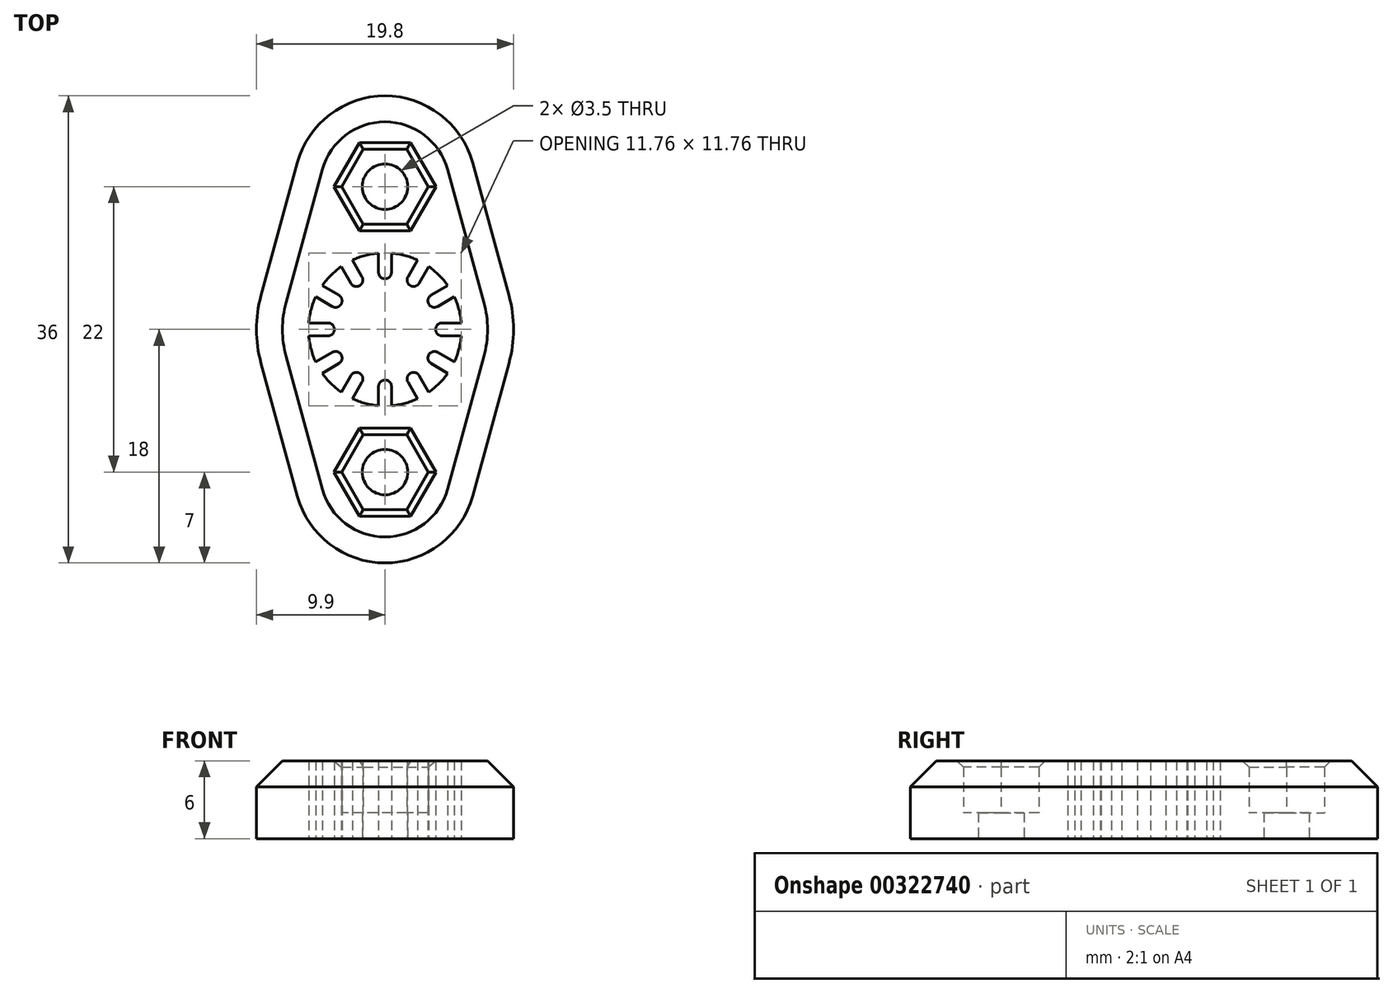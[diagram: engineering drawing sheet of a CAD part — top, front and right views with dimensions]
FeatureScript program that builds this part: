
annotation { "Feature Type Name" : "Feature", "Feature Type Description" : "" }
export const myFeature = defineFeature(function(context is Context, id is Id, definition is map)
    precondition{}
    {
        {
            assignVariable(context, id + "F0", {"name" : "teeth", "anyValue" : 12});
        }
        {
            assignVariable(context, id + "F1", {"name" : "height", "anyValue" : 6});
        }
        {
            var Q0;
            Q0=qCreatedBy(makeId("Top.planeOp"),FACE);
            var sketch = newSketch(context, id + "F2", { "sketchPlane" : qUnion([Q0])});
            skCircle(sketch, "E0", {"center": v(0, 0) * mm, "radius": 5.9 * mm});
            skArc(sketch, "E1", {"start": v(9.55, -2.61) * mm, "mid": v(9.9, 0) * mm, "end": v(9.55, 2.61) * mm});
            skArc(sketch, "E2", {"start": v(-6.75, 12.85) * mm, "mid": v(-4.25, 16.56) * mm, "end": v(0, 18) * mm});
            skLineSegment(sketch, "E3", {"start": v(-9.55, 2.6) * mm, "end": v(-6.75, 12.85) * mm});
            skArc(sketch, "E4.MirrorCS", {"start": v(6.75, 12.85) * mm, "mid": v(4.25, 16.56) * mm, "end": v(0, 18) * mm});
            skLineSegment(sketch, "E5.MirrorCS", {"start": v(9.55, 2.6) * mm, "end": v(6.75, 12.85) * mm});
            skLineSegment(sketch, "E6.MirrorCS", {"start": v(-9.55, -2.6) * mm, "end": v(-6.75, -12.85) * mm});
            skArc(sketch, "E7.MirrorCS", {"start": v(-6.75, -12.85) * mm, "mid": v(-4.25, -16.56) * mm, "end": v(0, -18) * mm});
            skArc(sketch, "E8.MirrorCS", {"start": v(6.75, -12.85) * mm, "mid": v(4.25, -16.56) * mm, "end": v(0, -18) * mm});
            skLineSegment(sketch, "E9.MirrorCS", {"start": v(9.55, -2.6) * mm, "end": v(6.75, -12.85) * mm});
            skArc(sketch, "E10.trimOffspring", {"start": v(-9.55, 2.61) * mm, "mid": v(-9.9, 0) * mm, "end": v(-9.55, -2.61) * mm});
            skCircle(sketch, "E11", {"center": v(0, 11) * mm, "radius": 1.75 * mm});
            skCircle(sketch, "E12.cCircle", {"center": v(0, 11) * mm, "radius": 2.9 * mm, "construction": true});
            skLineSegment(sketch, "E12.0", {"start": v(1.67, 8.1) * mm, "end": v(-1.67, 8.1) * mm});
            skLineSegment(sketch, "E12.1", {"start": v(-1.67, 8.1) * mm, "end": v(-3.35, 11) * mm});
            skLineSegment(sketch, "E12.2", {"start": v(-3.35, 11) * mm, "end": v(-1.67, 13.9) * mm});
            skLineSegment(sketch, "E12.3", {"start": v(-1.67, 13.9) * mm, "end": v(1.67, 13.9) * mm});
            skLineSegment(sketch, "E12.4", {"start": v(1.67, 13.9) * mm, "end": v(3.35, 11) * mm});
            skLineSegment(sketch, "E12.5", {"start": v(3.35, 11) * mm, "end": v(1.67, 8.1) * mm});
            skPoint(sketch, "E12.0.midPoint", {"position": v(0, 8.1) * mm});
            skLineSegment(sketch, "E13.MirrorCS", {"start": v(-1.67, -13.9) * mm, "end": v(1.67, -13.9) * mm});
            skLineSegment(sketch, "E14.MirrorCS", {"start": v(3.35, -11) * mm, "end": v(1.67, -8.1) * mm});
            skPoint(sketch, "E15.MirrorP", {"position": v(0, -8.1) * mm});
            skCircle(sketch, "E16.MirrorC", {"center": v(0, -11) * mm, "radius": 2.9 * mm, "construction": true});
            skCircle(sketch, "E17.MirrorC", {"center": v(0, -11) * mm, "radius": 1.75 * mm});
            skLineSegment(sketch, "E18.MirrorCS", {"start": v(1.67, -13.9) * mm, "end": v(3.35, -11) * mm});
            skLineSegment(sketch, "E19.MirrorCS", {"start": v(-1.67, -8.1) * mm, "end": v(-3.35, -11) * mm});
            skLineSegment(sketch, "E20.MirrorCS", {"start": v(-3.35, -11) * mm, "end": v(-1.67, -13.9) * mm});
            skLineSegment(sketch, "E21.MirrorCS", {"start": v(1.67, -8.1) * mm, "end": v(-1.67, -8.1) * mm});
            skSolve(sketch);
        }
        {
            var Q0;
            Q0=makeQuery(id+"F2.imprint","IMPRINT",FACE,{"disambiguationData":[TD([[makeQuery(id+"F2.imprint","IMPRINT",EDGE,{"derivedFrom":sQuery(id+"F2.wireOp",EDGE,"E0")}),-1.0]])]});
            extrude(context, id + "F3", {"entities" : qUnion([Q0]), "depth" : (getVariable(context, 'height')) * mm, "offsetDistance" : 25 * mm});
        }
        {
            var Q0;
            Q0=makeQuery(id+"F2.imprint","IMPRINT",FACE,{"disambiguationData":[TD([[makeQuery(id+"F2.imprint","IMPRINT",EDGE,{"derivedFrom":sQuery(id+"F2.wireOp",EDGE,"E11")}),-1.0]])]});
            var Q1;
            Q1=makeQuery(id+"F2.imprint","IMPRINT",FACE,{"disambiguationData":[TD([[makeQuery(id+"F2.imprint","IMPRINT",EDGE,{"derivedFrom":sQuery(id+"F2.wireOp",EDGE,"E13.MirrorCS")}),1.0]])]});
            extrude(context, id + "F4", {"entities" : qUnion([Q0, Q1]), "operationType" : NewBodyOperationType.ADD, "depth" : 2 * mm, "offsetDistance" : 25 * mm});
        }
        {
            var Q0;
            Q0=qCreatedBy(makeId("Top.planeOp"),FACE);
            var sketch = newSketch(context, id + "F5", { "sketchPlane" : qUnion([Q0])});
            skArc(sketch, "E22", {"start": v(0.5, -4.4) * mm, "mid": v(0, -3.9) * mm, "end": v(-0.5, -4.4) * mm});
            skLineSegment(sketch, "E23", {"start": v(0.5, -4.4) * mm, "end": v(0.5, -5.88) * mm});
            skLineSegment(sketch, "E24.MirrorCS", {"start": v(-0.5, -4.4) * mm, "end": v(-0.5, -5.88) * mm});
            skPoint(sketch, "E25", {"position": v(0, -5.9) * mm});
            skArc(sketch, "E26", {"start": v(-0.5, -5.88) * mm, "mid": v(0, -5.9) * mm, "end": v(0.5, -5.88) * mm});
            skPoint(sketch, "E27", {"position": v(0, -3.9) * mm});
            skSolve(sketch);
        }
        {
            var Q0;
            Q0=makeQuery(id+"F5.imprint","IMPRINT",FACE,{"disambiguationData":[TD([[makeQuery(id+"F5.imprint","IMPRINT",EDGE,{"derivedFrom":sQuery(id+"F5.wireOp",EDGE,"E22")}),1.0]])]});
            var Q1;
            Q1=makeQuery(id+"F3.opExtrude","CAP_FACE",FACE,{"disambiguationData":[OSD([sQuery(id+"F2.wireOp",EDGE,"E0"),sQuery(id+"F2.wireOp",EDGE,"E1"),sQuery(id+"F2.wireOp",EDGE,"E2"),sQuery(id+"F2.wireOp",EDGE,"E3"),sQuery(id+"F2.wireOp",EDGE,"E4.MirrorCS"),sQuery(id+"F2.wireOp",EDGE,"E5.MirrorCS"),sQuery(id+"F2.wireOp",EDGE,"E6.MirrorCS"),sQuery(id+"F2.wireOp",EDGE,"E7.MirrorCS"),sQuery(id+"F2.wireOp",EDGE,"E8.MirrorCS"),sQuery(id+"F2.wireOp",EDGE,"E9.MirrorCS"),sQuery(id+"F2.wireOp",EDGE,"E10.trimOffspring"),sQuery(id+"F2.wireOp",EDGE,"E12.0"),sQuery(id+"F2.wireOp",EDGE,"E12.1"),sQuery(id+"F2.wireOp",EDGE,"E12.2"),sQuery(id+"F2.wireOp",EDGE,"E12.3"),sQuery(id+"F2.wireOp",EDGE,"E12.4"),sQuery(id+"F2.wireOp",EDGE,"E12.5"),sQuery(id+"F2.wireOp",EDGE,"E13.MirrorCS"),sQuery(id+"F2.wireOp",EDGE,"E14.MirrorCS"),sQuery(id+"F2.wireOp",EDGE,"E18.MirrorCS"),sQuery(id+"F2.wireOp",EDGE,"E19.MirrorCS"),sQuery(id+"F2.wireOp",EDGE,"E20.MirrorCS"),sQuery(id+"F2.wireOp",EDGE,"E21.MirrorCS")])],"isStart":false});
            extrude(context, id + "F6", {"entities" : qUnion([Q0]), "endBound" : BoundingType.UP_TO_SURFACE, "depth" : 25 * mm, "endBoundEntityFace" : qUnion([Q1]), "offsetDistance" : 25 * mm});
        }
        {
            var Q0;
            Q0=qCreatedBy(makeId("Right.planeOp"),FACE);
            var sketch = newSketch(context, id + "F7", { "sketchPlane" : qUnion([Q0])});
            skLineSegment(sketch, "E28", {"start": v(0, 0) * mm, "end": v(0, 16.2) * mm, "construction": true});
            skSolve(sketch);
        }
        {
            var Q0;
            Q0=makeQuery(id+"F6.opExtrude","SWEPT_BODY",BODY,{"disambiguationData":[OSD([sQuery(id+"F5.wireOp",EDGE,"E22"),sQuery(id+"F5.wireOp",EDGE,"E23"),sQuery(id+"F5.wireOp",EDGE,"E24.MirrorCS"),sQuery(id+"F5.wireOp",EDGE,"E26")])]});
            var Q1;
            Q1=sQuery(id+"F7.wireOp",EDGE,"E28");
            circularPattern(context, id + "F8", {"operationType" : NewBodyOperationType.ADD, "entities" : qUnion([Q0]), "axis" : qUnion([Q1]), "angle" : 360 * degree, "instanceCount" : getVariable(context, 'teeth'), "equalSpace" : true, "computeTransformsWithoutBuiltin" : true});
        }
        {
            var Q0;
            Q0=makeQuery(id+"F3.opExtrude","CAP_EDGE",EDGE,{"disambiguationData":[OSD([sQuery(id+"F2.wireOp",EDGE,"E7.MirrorCS"),sQuery(id+"F2.wireOp",EDGE,"E8.MirrorCS")])],"isStart":false});
            chamfer(context, id + "F9", {"entities" : qUnion([Q0]), "width" : 2 * mm, "tangentPropagation" : true});
        }
        {
            var Q0;
            Q0=makeQuery(id+"F3.opExtrude","CAP_EDGE",EDGE,{"disambiguationData":[OSD([sQuery(id+"F2.wireOp",EDGE,"E20.MirrorCS")])],"isStart":false});
            var Q1;
            Q1=makeQuery(id+"F3.opExtrude","CAP_EDGE",EDGE,{"disambiguationData":[OSD([sQuery(id+"F2.wireOp",EDGE,"E19.MirrorCS")])],"isStart":false});
            var Q2;
            Q2=makeQuery(id+"F3.opExtrude","CAP_EDGE",EDGE,{"disambiguationData":[OSD([sQuery(id+"F2.wireOp",EDGE,"E21.MirrorCS")])],"isStart":false});
            var Q3;
            Q3=makeQuery(id+"F3.opExtrude","CAP_EDGE",EDGE,{"disambiguationData":[OSD([sQuery(id+"F2.wireOp",EDGE,"E14.MirrorCS")])],"isStart":false});
            var Q4;
            Q4=makeQuery(id+"F3.opExtrude","CAP_EDGE",EDGE,{"disambiguationData":[OSD([sQuery(id+"F2.wireOp",EDGE,"E18.MirrorCS")])],"isStart":false});
            var Q5;
            Q5=makeQuery(id+"F3.opExtrude","CAP_EDGE",EDGE,{"disambiguationData":[OSD([sQuery(id+"F2.wireOp",EDGE,"E13.MirrorCS")])],"isStart":false});
            var Q6;
            Q6=makeQuery(id+"F3.opExtrude","CAP_EDGE",EDGE,{"disambiguationData":[OSD([sQuery(id+"F2.wireOp",EDGE,"E12.0")])],"isStart":false});
            var Q7;
            Q7=makeQuery(id+"F3.opExtrude","CAP_EDGE",EDGE,{"disambiguationData":[OSD([sQuery(id+"F2.wireOp",EDGE,"E12.1")])],"isStart":false});
            var Q8;
            Q8=makeQuery(id+"F3.opExtrude","CAP_EDGE",EDGE,{"disambiguationData":[OSD([sQuery(id+"F2.wireOp",EDGE,"E12.2")])],"isStart":false});
            var Q9;
            Q9=makeQuery(id+"F3.opExtrude","CAP_EDGE",EDGE,{"disambiguationData":[OSD([sQuery(id+"F2.wireOp",EDGE,"E12.3")])],"isStart":false});
            var Q10;
            Q10=makeQuery(id+"F3.opExtrude","CAP_EDGE",EDGE,{"disambiguationData":[OSD([sQuery(id+"F2.wireOp",EDGE,"E12.4")])],"isStart":false});
            var Q11;
            Q11=makeQuery(id+"F3.opExtrude","CAP_EDGE",EDGE,{"disambiguationData":[OSD([sQuery(id+"F2.wireOp",EDGE,"E12.5")])],"isStart":false});
            chamfer(context, id + "F10", {"entities" : qUnion([Q0, Q1, Q2, Q3, Q4, Q5, Q6, Q7, Q8, Q9, Q10, Q11]), "width" : 0.5 * mm, "tangentPropagation" : true});
        }
    });
